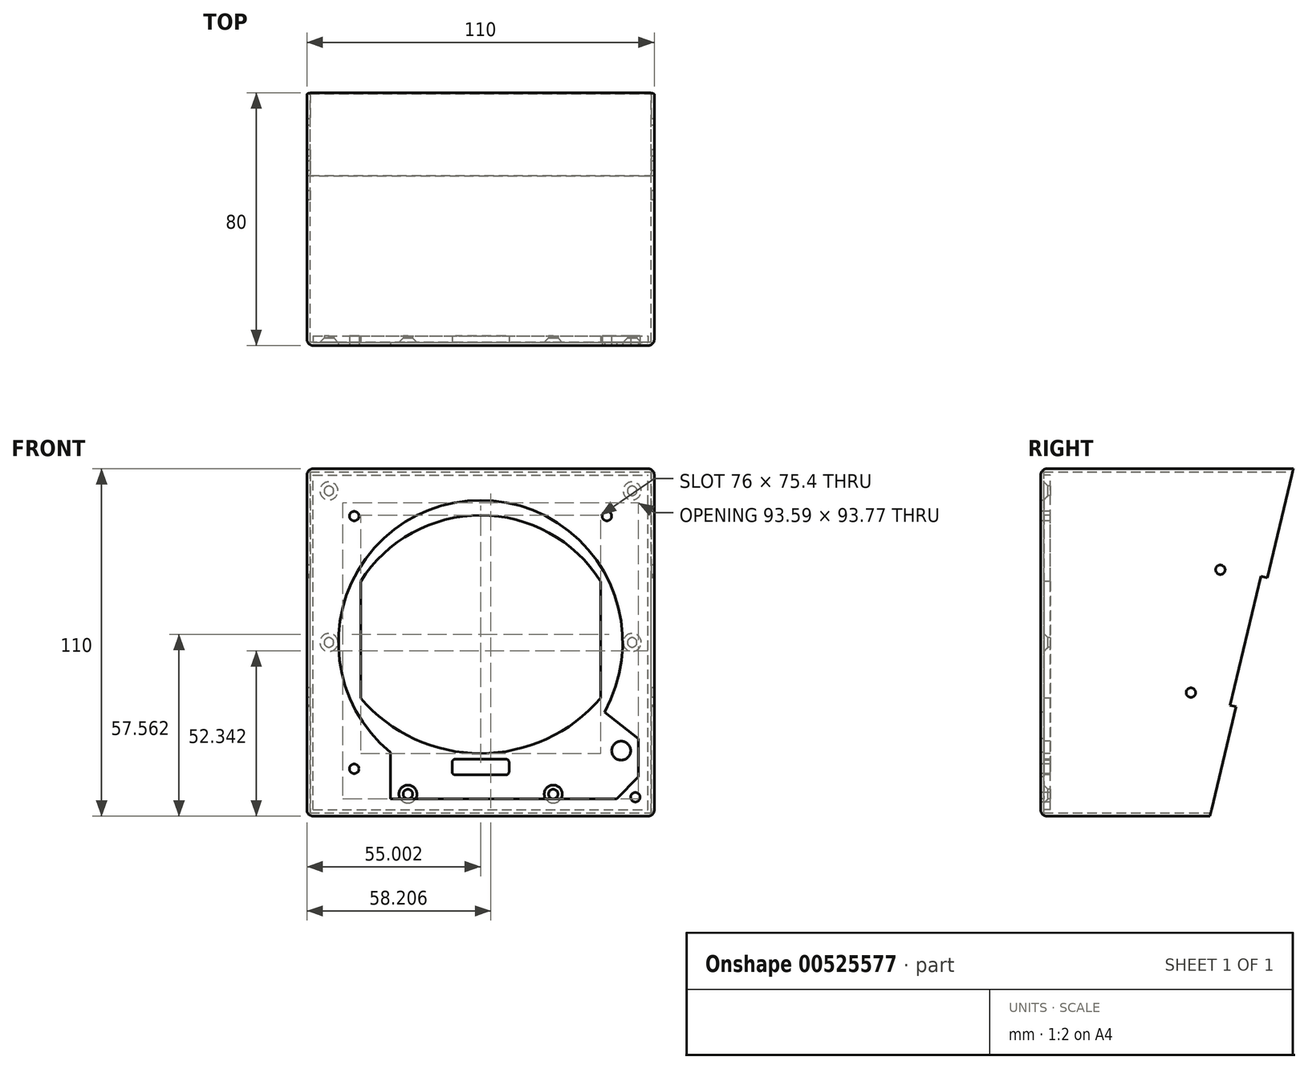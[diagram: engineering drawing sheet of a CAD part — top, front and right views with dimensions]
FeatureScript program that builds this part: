
annotation { "Feature Type Name" : "Feature", "Feature Type Description" : "" }
export const myFeature = defineFeature(function(context is Context, id is Id, definition is map)
    precondition{}
    {
        {
            var Q0;
            Q0=qCreatedBy(makeId("Front.planeOp"),FACE);
            var sketch = newSketch(context, id + "F0", { "sketchPlane" : qUnion([Q0])});
            skLineSegment(sketch, "E0.bottom", {"start": v(-56.84, -55) * mm, "end": v(-166.84, -55) * mm});
            skLineSegment(sketch, "E0.top", {"start": v(-56.84, 55) * mm, "end": v(-166.84, 55) * mm});
            skLineSegment(sketch, "E0.left", {"start": v(-56.84, -55) * mm, "end": v(-56.84, 55) * mm});
            skLineSegment(sketch, "E0.right", {"start": v(-166.84, -55) * mm, "end": v(-166.84, 55) * mm});
            skPoint(sketch, "E0.middle", {"position": v(-111.84, 0) * mm});
            skSolve(sketch);
        }
        {
            var Q0;
            Q0=makeQuery(id+"F0.imprint","IMPRINT",FACE,{"disambiguationData":[TD([[makeQuery(id+"F0.imprint","IMPRINT",EDGE,{"derivedFrom":sQuery(id+"F0.wireOp",EDGE,"E0.bottom")}),-1.0]])]});
            extrude(context, id + "F1", {"entities" : qUnion([Q0]), "endBound" : BoundingType.SYMMETRIC, "depth" : 120 * mm});
        }
        {
            var Q0;
            Q0=makeQuery(id+"F1.opExtrude","CAP_FACE",FACE,{"disambiguationData":[OSD([sQuery(id+"F0.wireOp",EDGE,"E0.bottom"),sQuery(id+"F0.wireOp",EDGE,"E0.top"),sQuery(id+"F0.wireOp",EDGE,"E0.left"),sQuery(id+"F0.wireOp",EDGE,"E0.right")])],"isStart":true});
            shell(context, id + "F2", {"entities" : qUnion([Q0]), "thickness" : 1 * mm});
        }
        {
            var Q0;
            Q0=makeQuery(id+"F1.opExtrude","SWEPT_FACE",FACE,{"disambiguationData":[OSD([sQuery(id+"F0.wireOp",EDGE,"E0.right")])]});
            var sketch = newSketch(context, id + "F3", { "sketchPlane" : qUnion([Q0])});
            skLineSegment(sketch, "E1", {"start": v(-20, 55) * mm, "end": v(6.4, -55) * mm});
            skLineSegment(sketch, "E2", {"start": v(6.4, -55) * mm, "end": v(-89.83, -55) * mm});
            skLineSegment(sketch, "E3", {"start": v(-89.83, -55) * mm, "end": v(-89.83, 55) * mm});
            skLineSegment(sketch, "E4", {"start": v(-89.83, 55) * mm, "end": v(-20, 55) * mm});
            skCircle(sketch, "E5", {"center": v(3.1, 23.01) * mm, "radius": 1.5 * mm});
            skCircle(sketch, "E6", {"center": v(12.44, -15.88) * mm, "radius": 1.5 * mm});
            skLineSegment(sketch, "E7", {"start": v(-6.81, 0.06) * mm, "end": v(32, 9.38) * mm, "construction": true});
            skLineSegment(sketch, "E8", {"start": v(-11.71, 20.48) * mm, "end": v(-1.9, -20.36) * mm});
            skLineSegment(sketch, "E9", {"start": v(-1.9, -20.36) * mm, "end": v(0.04, -19.9) * mm});
            skLineSegment(sketch, "E10", {"start": v(0.04, -19.9) * mm, "end": v(-9.77, 20.95) * mm});
            skLineSegment(sketch, "E11", {"start": v(-9.77, 20.95) * mm, "end": v(-11.71, 20.48) * mm});
            skSolve(sketch);
        }
        {
            var Q0;
            Q0=qSketchRegion(id+"F3",true);
            extrude(context, id + "F4", {"entities" : qUnion([Q0]), "operationType" : NewBodyOperationType.REMOVE, "oppositeDirection" : true, "depth" : 110 * mm});
        }
        {
            var Q0;
            Q0=makeQuery(id+"F1.opExtrude","CAP_EDGE",EDGE,{"disambiguationData":[OSD([sQuery(id+"F0.wireOp",EDGE,"E0.right")])],"isStart":false});
            var Q1;
            Q1=makeQuery(id+"F1.opExtrude","SWEPT_EDGE",EDGE,{"disambiguationData":[OSD([sQuery(id+"F0.wireOp",EDGE,"E0.top"),sQuery(id+"F0.wireOp",EDGE,"E0.right")])]});
            var Q2;
            Q2=makeQuery(id+"F1.opExtrude","CAP_EDGE",EDGE,{"disambiguationData":[OSD([sQuery(id+"F0.wireOp",EDGE,"E0.top")])],"isStart":false});
            var Q3;
            Q3=makeQuery(id+"F1.opExtrude","CAP_EDGE",EDGE,{"disambiguationData":[OSD([sQuery(id+"F0.wireOp",EDGE,"E0.left")])],"isStart":false});
            var Q4;
            Q4=makeQuery(id+"F1.opExtrude","SWEPT_EDGE",EDGE,{"disambiguationData":[OSD([sQuery(id+"F0.wireOp",EDGE,"E0.top"),sQuery(id+"F0.wireOp",EDGE,"E0.left")])]});
            var Q5;
            Q5=makeQuery(id+"F1.opExtrude","CAP_EDGE",EDGE,{"disambiguationData":[OSD([sQuery(id+"F0.wireOp",EDGE,"E0.bottom")])],"isStart":false});
            var Q6;
            Q6=makeQuery(id+"F1.opExtrude","SWEPT_EDGE",EDGE,{"disambiguationData":[OSD([sQuery(id+"F0.wireOp",EDGE,"E0.bottom"),sQuery(id+"F0.wireOp",EDGE,"E0.left")])]});
            var Q7;
            Q7=makeQuery(id+"F1.opExtrude","SWEPT_EDGE",EDGE,{"disambiguationData":[OSD([sQuery(id+"F0.wireOp",EDGE,"E0.bottom"),sQuery(id+"F0.wireOp",EDGE,"E0.right")])]});
            fillet(context, id + "F5", {"entities" : qUnion([Q0, Q1, Q2, Q3, Q4, Q5, Q6, Q7]), "radius" : 2 * mm, "tangentPropagation" : true, "allowEdgeOverflow" : false});
        }
        {
            var Q0;
            Q0=makeQuery(id+"F1.opExtrude","CAP_FACE",FACE,{"disambiguationData":[OSD([sQuery(id+"F0.wireOp",EDGE,"E0.bottom"),sQuery(id+"F0.wireOp",EDGE,"E0.top"),sQuery(id+"F0.wireOp",EDGE,"E0.left"),sQuery(id+"F0.wireOp",EDGE,"E0.right")])],"isStart":false});
            var sketch = newSketch(context, id + "F6", { "sketchPlane" : qUnion([Q0])});
            skCircle(sketch, "E12", {"center": v(-111.84, 0) * mm, "radius": 45 * mm});
            skLineSegment(sketch, "E13", {"start": v(-140.4, -34.77) * mm, "end": v(-140.4, -49.54) * mm});
            skLineSegment(sketch, "E14", {"start": v(-140.4, -49.54) * mm, "end": v(-68.8, -49.54) * mm});
            skLineSegment(sketch, "E15", {"start": v(-68.8, -49.54) * mm, "end": v(-61.84, -42.48) * mm});
            skLineSegment(sketch, "E16", {"start": v(-61.84, -42.48) * mm, "end": v(-61.84, -30.48) * mm});
            skLineSegment(sketch, "E17", {"start": v(-61.84, -30.48) * mm, "end": v(-72.6, -22.03) * mm});
            skCircle(sketch, "E18", {"center": v(-151.84, 40) * mm, "radius": 1.5 * mm});
            skCircle(sketch, "E19", {"center": v(-71.84, 40) * mm, "radius": 1.5 * mm});
            skCircle(sketch, "E20", {"center": v(-151.84, -40) * mm, "radius": 1.5 * mm});
            skCircle(sketch, "E21", {"center": v(-62.84, -49) * mm, "radius": 1.5 * mm});
            skSolve(sketch);
        }
        {
            var Q0;
            Q0=qSketchRegion(id+"F6",true);
            extrude(context, id + "F7", {"entities" : qUnion([Q0]), "operationType" : NewBodyOperationType.REMOVE, "oppositeDirection" : true, "depth" : 1 * mm});
        }
        {
            var Q0;
            Q0=makeQuery(id+"F2.opShell","OFFSET_FACE",FACE,{"disambiguationData":[OSD([sQuery(id+"F0.wireOp",EDGE,"E0.bottom"),sQuery(id+"F0.wireOp",EDGE,"E0.top"),sQuery(id+"F0.wireOp",EDGE,"E0.left"),sQuery(id+"F0.wireOp",EDGE,"E0.right")])]});
            var sketch = newSketch(context, id + "F8", { "sketchPlane" : qUnion([Q0])});
            skLineSegment(sketch, "E22.bottom", {"start": v(164.84, -53) * mm, "end": v(58.84, -53) * mm});
            skLineSegment(sketch, "E22.top", {"start": v(164.84, 53) * mm, "end": v(58.84, 53) * mm});
            skLineSegment(sketch, "E22.left", {"start": v(164.84, -53) * mm, "end": v(164.84, 53) * mm});
            skLineSegment(sketch, "E22.right", {"start": v(58.84, -53) * mm, "end": v(58.84, 53) * mm});
            skPoint(sketch, "E22.middle", {"position": v(111.84, 0) * mm});
            skLineSegment(sketch, "E23", {"start": v(73.84, 19.37) * mm, "end": v(73.84, -17.63) * mm});
            skLineSegment(sketch, "E24", {"start": v(149.84, 19.37) * mm, "end": v(149.84, -17.63) * mm});
            skArc(sketch, "E25", {"start": v(149.84, 19.37) * mm, "mid": v(111.84, 40.26) * mm, "end": v(73.84, 19.37) * mm});
            skArc(sketch, "E26", {"start": v(73.84, -17.63) * mm, "mid": v(111.84, -35.14) * mm, "end": v(149.84, -17.63) * mm});
            skLineSegment(sketch, "E27.bottom", {"start": v(103.84, -36.95) * mm, "end": v(119.84, -36.95) * mm});
            skLineSegment(sketch, "E27.top", {"start": v(103.84, -41.95) * mm, "end": v(119.84, -41.95) * mm});
            skLineSegment(sketch, "E27.left", {"start": v(102.84, -37.95) * mm, "end": v(102.84, -40.95) * mm});
            skLineSegment(sketch, "E27.right", {"start": v(120.84, -37.95) * mm, "end": v(120.84, -40.95) * mm});
            skPoint(sketch, "E28.visualSharp", {"position": v(102.84, -36.95) * mm});
            skArc(sketch, "E28.filletArc", {"start": v(103.84, -36.95) * mm, "mid": v(103.13, -37.24) * mm, "end": v(102.84, -37.95) * mm});
            skPoint(sketch, "E29.visualSharp", {"position": v(102.84, -41.95) * mm});
            skArc(sketch, "E29.filletArc", {"start": v(102.84, -40.95) * mm, "mid": v(103.13, -41.65) * mm, "end": v(103.84, -41.95) * mm});
            skPoint(sketch, "E30.visualSharp", {"position": v(120.84, -36.95) * mm});
            skArc(sketch, "E30.filletArc", {"start": v(120.84, -37.95) * mm, "mid": v(120.55, -37.24) * mm, "end": v(119.84, -36.95) * mm});
            skPoint(sketch, "E31.visualSharp", {"position": v(120.84, -41.95) * mm});
            skArc(sketch, "E31.filletArc", {"start": v(119.84, -41.95) * mm, "mid": v(120.55, -41.65) * mm, "end": v(120.84, -40.95) * mm});
            skPoint(sketch, "E32", {"position": v(111.84, -39.45) * mm});
            skCircle(sketch, "E33", {"center": v(151.84, 40) * mm, "radius": 1.5 * mm});
            skCircle(sketch, "E34", {"center": v(71.84, 40) * mm, "radius": 1.5 * mm});
            skCircle(sketch, "E35", {"center": v(62.84, -49) * mm, "radius": 1.5 * mm});
            skCircle(sketch, "E36", {"center": v(151.84, -40) * mm, "radius": 1.5 * mm});
            skCircle(sketch, "E37", {"center": v(67.34, -34.27) * mm, "radius": 3 * mm});
            skSolve(sketch);
        }
        {
            var Q0;
            Q0=qSketchRegion(id+"F8",true);
            extrude(context, id + "F9", {"entities" : qUnion([Q0]), "depth" : 2 * mm});
        }
        {
            var Q0;
            Q0=makeQuery(id+"F9.opExtrude","CAP_FACE",FACE,{"disambiguationData":[OSD([sQuery(id+"F8.wireOp",EDGE,"E22.bottom"),sQuery(id+"F8.wireOp",EDGE,"E22.top"),sQuery(id+"F8.wireOp",EDGE,"E22.left"),sQuery(id+"F8.wireOp",EDGE,"E22.right"),sQuery(id+"F8.wireOp",EDGE,"E23"),sQuery(id+"F8.wireOp",EDGE,"E24"),sQuery(id+"F8.wireOp",EDGE,"E25"),sQuery(id+"F8.wireOp",EDGE,"E26"),sQuery(id+"F8.wireOp",EDGE,"E27.bottom"),sQuery(id+"F8.wireOp",EDGE,"E27.top"),sQuery(id+"F8.wireOp",EDGE,"E27.left"),sQuery(id+"F8.wireOp",EDGE,"E27.right"),sQuery(id+"F8.wireOp",EDGE,"E28.filletArc"),sQuery(id+"F8.wireOp",EDGE,"E29.filletArc"),sQuery(id+"F8.wireOp",EDGE,"E30.filletArc"),sQuery(id+"F8.wireOp",EDGE,"E31.filletArc"),sQuery(id+"F8.wireOp",EDGE,"E33"),sQuery(id+"F8.wireOp",EDGE,"E34"),sQuery(id+"F8.wireOp",EDGE,"E35"),sQuery(id+"F8.wireOp",EDGE,"E36"),sQuery(id+"F8.wireOp",EDGE,"E37")])],"isStart":true});
            var sketch = newSketch(context, id + "F10", { "sketchPlane" : qUnion([Q0])});
            skLineSegment(sketch, "E38.bottom", {"start": v(-72.84, -43) * mm, "end": v(-150.84, -43) * mm});
            skLineSegment(sketch, "E38.top", {"start": v(-72.84, 43) * mm, "end": v(-150.84, 43) * mm});
            skLineSegment(sketch, "E38.left", {"start": v(-72.84, -43) * mm, "end": v(-72.84, 43) * mm});
            skLineSegment(sketch, "E38.right", {"start": v(-150.84, -43) * mm, "end": v(-150.84, 43) * mm});
            skPoint(sketch, "E38.middle", {"position": v(-111.84, 0) * mm});
            skLineSegment(sketch, "E39.bottom", {"start": v(-56.84, -55) * mm, "end": v(-166.84, -55) * mm});
            skLineSegment(sketch, "E39.top", {"start": v(-56.84, 55) * mm, "end": v(-166.84, 55) * mm});
            skLineSegment(sketch, "E39.left", {"start": v(-56.84, -55) * mm, "end": v(-56.84, 55) * mm});
            skLineSegment(sketch, "E39.right", {"start": v(-166.84, -55) * mm, "end": v(-166.84, 55) * mm});
            skSolve(sketch);
        }
        {
            var Q0;
            {var subQ10=sQuery(id+"F10.wireOp",EDGE,"E38.bottom");Q0=makeQuery(id+"F10.imprint","IMPRINT",FACE,{"disambiguationData":[TD([[makeQuery(id+"F10.imprint","IMPRINT",EDGE,{"derivedFrom":subQ10}),1.0]])]});}
            var sketch = newSketch(context, id + "F11", { "sketchPlane" : qUnion([Q0])});
            skCircle(sketch, "E40", {"center": v(-159.84, 48) * mm, "radius": 1.5 * mm});
            skCircle(sketch, "E41", {"center": v(-63.84, 48) * mm, "radius": 1.5 * mm});
            skCircle(sketch, "E42", {"center": v(-88.84, -48) * mm, "radius": 1.5 * mm});
            skCircle(sketch, "E43", {"center": v(-134.84, -48) * mm, "radius": 1.5 * mm});
            skCircle(sketch, "E44", {"center": v(-159.84, 0) * mm, "radius": 1.5 * mm});
            skCircle(sketch, "E45", {"center": v(-63.84, 0) * mm, "radius": 1.5 * mm});
            skSolve(sketch);
        }
        {
            var Q0;
            Q0=sQuery(id+"F11.wireOp",VERTEX,"E43.center");
            var Q1;
            Q1=sQuery(id+"F11.wireOp",VERTEX,"E42.center");
            var Q2;
            Q2=sQuery(id+"F11.wireOp",VERTEX,"E40.center");
            var Q3;
            Q3=sQuery(id+"F11.wireOp",VERTEX,"E41.center");
            var Q4;
            Q4=sQuery(id+"F11.wireOp",VERTEX,"E44.center");
            var Q5;
            Q5=sQuery(id+"F11.wireOp",VERTEX,"E45.center");
            var Q6;
            Q6=makeQuery(id+"F9.opExtrude","SWEPT_BODY",BODY,{"disambiguationData":[OSD([sQuery(id+"F8.wireOp",EDGE,"E22.bottom"),sQuery(id+"F8.wireOp",EDGE,"E22.top"),sQuery(id+"F8.wireOp",EDGE,"E22.left"),sQuery(id+"F8.wireOp",EDGE,"E22.right"),sQuery(id+"F8.wireOp",EDGE,"E23"),sQuery(id+"F8.wireOp",EDGE,"E24"),sQuery(id+"F8.wireOp",EDGE,"E25"),sQuery(id+"F8.wireOp",EDGE,"E26"),sQuery(id+"F8.wireOp",EDGE,"E27.bottom"),sQuery(id+"F8.wireOp",EDGE,"E27.top"),sQuery(id+"F8.wireOp",EDGE,"E27.left"),sQuery(id+"F8.wireOp",EDGE,"E27.right"),sQuery(id+"F8.wireOp",EDGE,"E28.filletArc"),sQuery(id+"F8.wireOp",EDGE,"E29.filletArc"),sQuery(id+"F8.wireOp",EDGE,"E30.filletArc"),sQuery(id+"F8.wireOp",EDGE,"E31.filletArc"),sQuery(id+"F8.wireOp",EDGE,"E33"),sQuery(id+"F8.wireOp",EDGE,"E34"),sQuery(id+"F8.wireOp",EDGE,"E35"),sQuery(id+"F8.wireOp",EDGE,"E36"),sQuery(id+"F8.wireOp",EDGE,"E37")])]});
            hole(context, id + "F12", {"style" : HoleStyle.C_SINK, "endStyle" : HoleEndStyle.THROUGH, "holeDiameter" : 3 * mm, "cSinkDiameter" : 5.7 * mm, "cSinkAngle" : 90 * degree, "locations" : qUnion([Q0, Q1, Q2, Q3, Q4, Q5]), "scope" : qUnion([Q6]), "isTappedThrough" : true});
        }
    });
